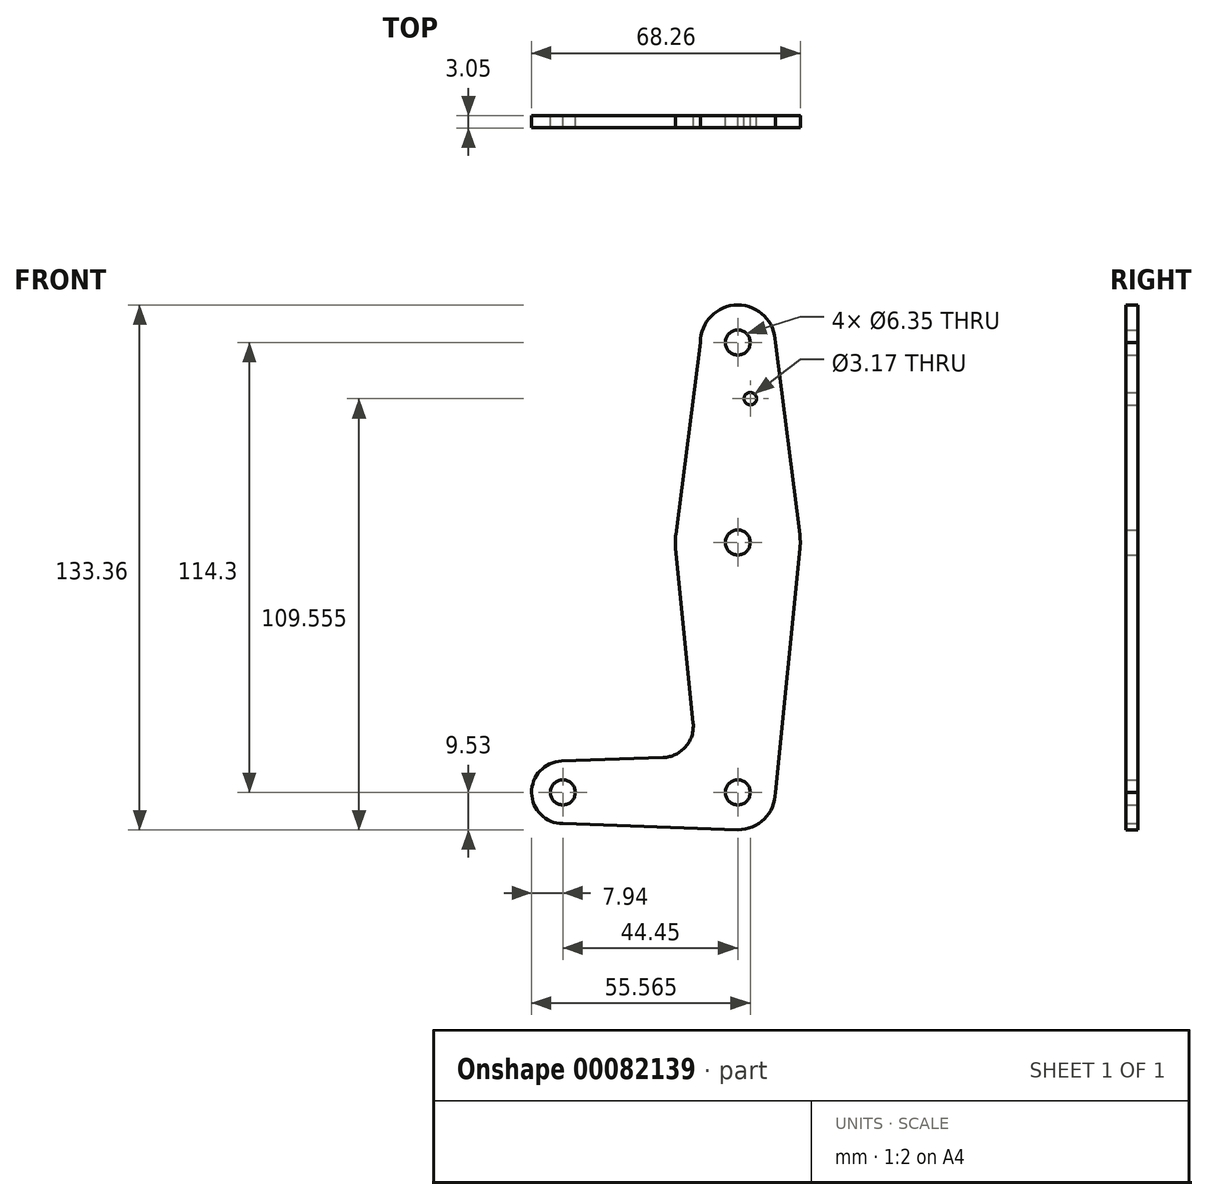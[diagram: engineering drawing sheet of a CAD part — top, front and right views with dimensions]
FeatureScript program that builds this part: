
annotation { "Feature Type Name" : "Feature", "Feature Type Description" : "" }
export const myFeature = defineFeature(function(context is Context, id is Id, definition is map)
    precondition{}
    {
        {
            var Q0;
            Q0=qCreatedBy(makeId("Front.planeOp"),FACE);
            var sketch = newSketch(context, id + "F0", { "sketchPlane" : qUnion([Q0])});
            skCircle(sketch, "E0", {"center": v(0, 0) * mm, "radius": 9.53 * mm});
            skCircle(sketch, "E1", {"center": v(-44.45, 0) * mm, "radius": 7.94 * mm});
            skCircle(sketch, "E2", {"center": v(0, 63.5) * mm, "radius": 15.88 * mm});
            skCircle(sketch, "E3", {"center": v(0, 114.3) * mm, "radius": 9.53 * mm});
            skLineSegment(sketch, "E4", {"start": v(0, 114.3) * mm, "end": v(0, 0) * mm, "construction": true});
            skLineSegment(sketch, "E5", {"start": v(0, 0) * mm, "end": v(-44.45, 0) * mm, "construction": true});
            skLineSegment(sketch, "E6", {"start": v(0, 40.23) * mm, "end": v(0, 85.71) * mm, "construction": true});
            skLineSegment(sketch, "E7", {"start": v(9.52, 114.3) * mm, "end": v(15.75, 65.5) * mm});
            skLineSegment(sketch, "E8", {"start": v(-9.52, 114.3) * mm, "end": v(-15.75, 65.5) * mm});
            skLineSegment(sketch, "E9", {"start": v(0, -9.52) * mm, "end": v(-44.45, -7.94) * mm});
            skCircle(sketch, "E10", {"center": v(0, 114.3) * mm, "radius": 3.18 * mm});
            skCircle(sketch, "E11", {"center": v(0, 63.5) * mm, "radius": 3.18 * mm});
            skCircle(sketch, "E12", {"center": v(0, 0) * mm, "radius": 3.18 * mm});
            skCircle(sketch, "E13", {"center": v(-44.45, 0) * mm, "radius": 3.18 * mm});
            skCircle(sketch, "E14", {"center": v(3.18, 100.03) * mm, "radius": 1.59 * mm});
            skLineSegment(sketch, "E15", {"start": v(15.8, 61.9) * mm, "end": v(9.52, 0) * mm});
            skLineSegment(sketch, "E16", {"start": v(-15.8, 61.91) * mm, "end": v(-11.34, 17.6) * mm});
            skLineSegment(sketch, "E17", {"start": v(-18.97, 8.85) * mm, "end": v(-44.73, 7.93) * mm});
            skArc(sketch, "E18.filletArc", {"start": v(-18.97, 8.85) * mm, "mid": v(-13.26, 11.57) * mm, "end": v(-11.34, 17.6) * mm});
            skSolve(sketch);
        }
        {
            var Q0;
            Q0=makeQuery(id+"F0.imprint","IMPRINT",FACE,{"disambiguationData":[TD([[makeQuery(id+"F0.imprint","IMPRINT",EDGE,{"derivedFrom":sQuery(id+"F0.wireOp",EDGE,"E11")}),-1.0]])]});
            var Q1;
            {var subQ5=sQuery(id+"F0.wireOp",EDGE,"E15");Q1=makeQuery(id+"F0.imprint","IMPRINT",FACE,{"disambiguationData":[TD([[makeQuery(id+"F0.imprint","IMPRINT",EDGE,{"derivedFrom":subQ5}),-1.0]])]});}
            var Q2;
            {var subQ1=sQuery(id+"F0.wireOp",EDGE,"E7");Q2=makeQuery(id+"F0.imprint","IMPRINT",FACE,{"disambiguationData":[TD([[makeQuery(id+"F0.imprint","IMPRINT",EDGE,{"derivedFrom":subQ1}),-1.0]])]});}
            var Q3;
            Q3=makeQuery(id+"F0.imprint","IMPRINT",FACE,{"disambiguationData":[TD([[makeQuery(id+"F0.imprint","IMPRINT",EDGE,{"derivedFrom":sQuery(id+"F0.wireOp",EDGE,"E10")}),-1.0]])]});
            var Q4;
            Q4=makeQuery(id+"F0.imprint","IMPRINT",FACE,{"disambiguationData":[TD([[makeQuery(id+"F0.imprint","IMPRINT",EDGE,{"derivedFrom":sQuery(id+"F0.wireOp",EDGE,"E12")}),-1.0]])]});
            var Q5;
            Q5=makeQuery(id+"F0.imprint","IMPRINT",FACE,{"disambiguationData":[TD([[makeQuery(id+"F0.imprint","IMPRINT",EDGE,{"derivedFrom":sQuery(id+"F0.wireOp",EDGE,"E13")}),-1.0]])]});
            extrude(context, id + "F1", {"entities" : qUnion([Q0, Q1, Q2, Q3, Q4, Q5]), "depth" : 3.05 * mm});
        }
    });
